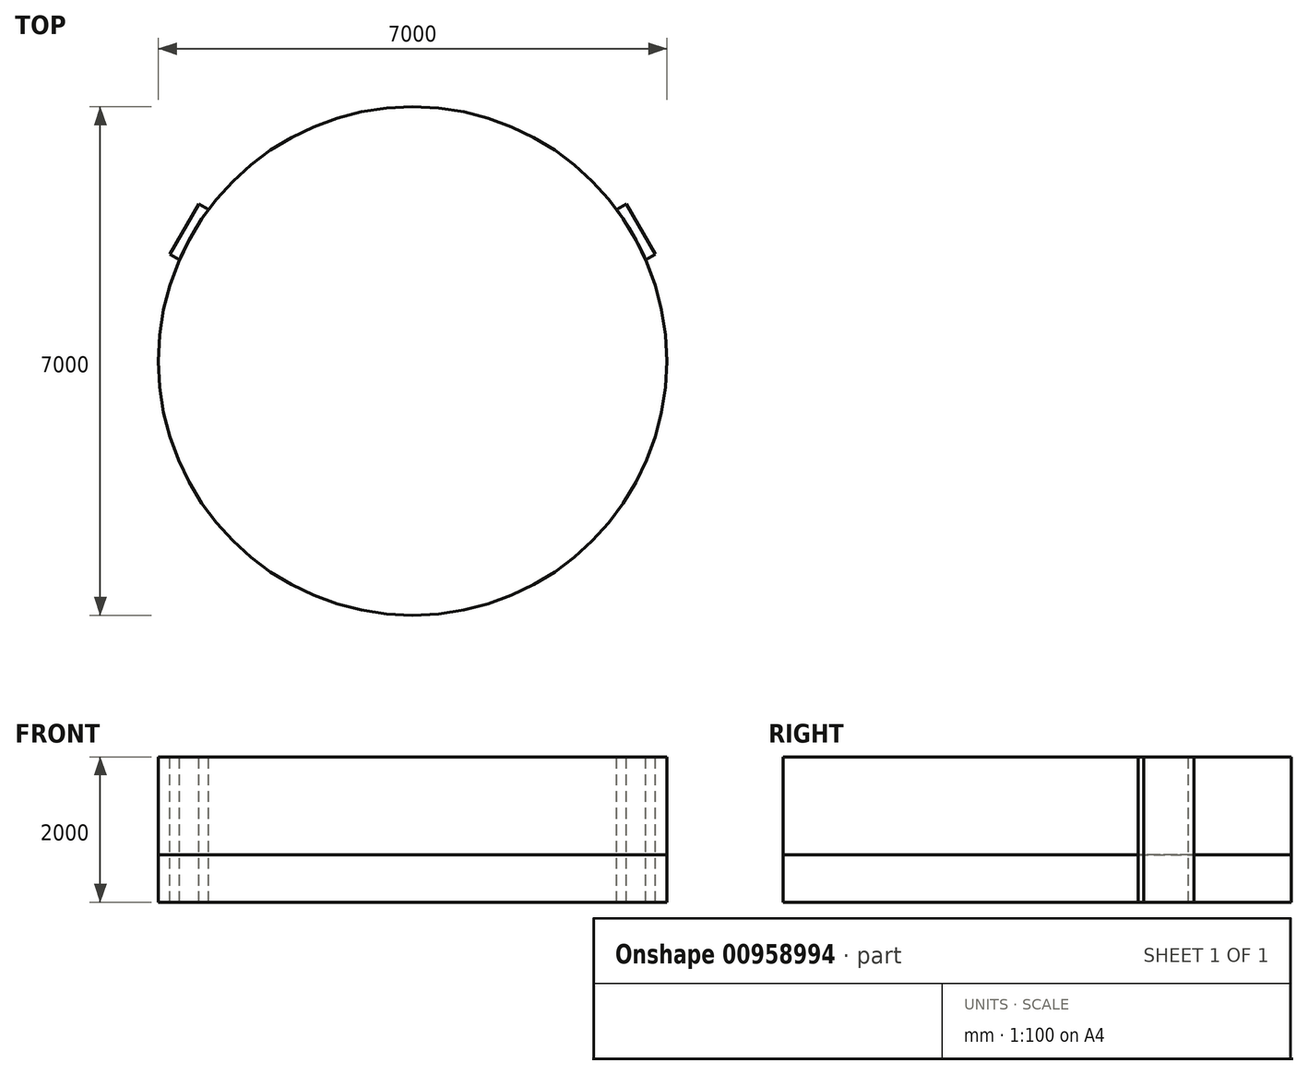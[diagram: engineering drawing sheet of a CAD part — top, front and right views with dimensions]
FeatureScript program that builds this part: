
annotation { "Feature Type Name" : "Feature", "Feature Type Description" : "" }
export const myFeature = defineFeature(function(context is Context, id is Id, definition is map)
    precondition{}
    {
        {
            var Q0;
            Q0=qCreatedBy(makeId("Top.planeOp"),FACE);
            var sketch = newSketch(context, id + "F0", { "sketchPlane" : qUnion([Q0])});
            skCircle(sketch, "E0", {"center": v(0, 0) * mm, "radius": 3500 * mm});
            skSolve(sketch);
        }
        {
            var Q0;
            Q0=makeQuery(id+"F0.imprint","IMPRINT",FACE,{"disambiguationData":[TD([[makeQuery(id+"F0.imprint","IMPRINT",EDGE,{"derivedFrom":sQuery(id+"F0.wireOp",EDGE,"E0")}),1.0]])]});
            extrude(context, id + "F1", {"entities" : qUnion([Q0]), "depth" : 1350 * mm, "offsetDistance" : 25 * mm});
        }
        {
            var Q0;
            Q0=makeQuery(id+"F1.opExtrude","CAP_FACE",FACE,{"disambiguationData":[OSD([sQuery(id+"F0.wireOp",EDGE,"E0")])],"isStart":false});
            var sketch = newSketch(context, id + "F2", { "sketchPlane" : qUnion([Q0])});
            skCircle(sketch, "E1", {"center": v(-852.5, -2750) * mm, "radius": 380 * mm});
            skLineSegment(sketch, "E2", {"start": v(-3911.37, 0) * mm, "end": v(4057.7, 0) * mm});
            skLineSegment(sketch, "E3", {"start": v(0, 3613.1) * mm, "end": v(0, -3590.58) * mm});
            skSolve(sketch);
        }
        {
            var Q0;
            Q0=sQuery(id+"F2.wireOp",EDGE,"E1");
            extrude(context, id + "F3", {"bodyType" : ToolBodyType.SURFACE, "surfaceEntities" : qUnion([Q0]), "depth" : 25 * mm, "offsetDistance" : 25 * mm});
        }
        {
            var Q0;
            Q0=makeQuery(id+"F1.opExtrude","CAP_FACE",FACE,{"disambiguationData":[OSD([sQuery(id+"F0.wireOp",EDGE,"E0")])],"isStart":false});
            var sketch = newSketch(context, id + "F4", { "sketchPlane" : qUnion([Q0])});
            skCircle(sketch, "E4", {"center": v(0, -3675.04) * mm, "radius": 110 * mm});
            skLineSegment(sketch, "E5", {"start": v(0, 3718.6) * mm, "end": v(0, -3971.3) * mm});
            skLineSegment(sketch, "E6", {"start": v(0, -3971.3) * mm, "end": v(4140.8, 0) * mm});
            skLineSegment(sketch, "E7", {"start": v(4140.8, 0) * mm, "end": v(-4000.44, 0) * mm});
            skSolve(sketch);
        }
        {
            var Q0;
            Q0=sQuery(id+"F4.wireOp",EDGE,"E4");
            extrude(context, id + "F5", {"bodyType" : ToolBodyType.SURFACE, "surfaceEntities" : qUnion([Q0]), "oppositeDirection" : true, "depth" : 2000 * mm, "offsetDistance" : 25 * mm});
        }
        {
            var Q0;
            Q0=makeQuery(id+"F1.opExtrude","CAP_FACE",FACE,{"disambiguationData":[OSD([sQuery(id+"F0.wireOp",EDGE,"E0")])],"isStart":false});
            var sketch = newSketch(context, id + "F6", { "sketchPlane" : qUnion([Q0])});
            skLineSegment(sketch, "E8", {"start": v(5183.48, 0) * mm, "end": v(-4726.63, 0) * mm});
            skLineSegment(sketch, "E9", {"start": v(0, 0) * mm, "end": v(4037.1, 2330.82) * mm});
            skLineSegment(sketch, "E10", {"start": v(0, 0) * mm, "end": v(-4709.99, 2719.31) * mm});
            skLineSegment(sketch, "E11", {"start": v(-2811.23, 2084.94) * mm, "end": v(-3211.23, 1392.12) * mm});
            skLineSegment(sketch, "E12", {"start": v(-3211.23, 1392.12) * mm, "end": v(-3341.13, 1467.12) * mm});
            skLineSegment(sketch, "E13", {"start": v(-3341.13, 1467.12) * mm, "end": v(-2941.13, 2159.94) * mm});
            skLineSegment(sketch, "E14", {"start": v(-2941.13, 2159.94) * mm, "end": v(-2811.23, 2084.94) * mm});
            skLineSegment(sketch, "E15", {"start": v(2811.23, 2084.94) * mm, "end": v(3211.23, 1392.12) * mm});
            skLineSegment(sketch, "E16", {"start": v(3211.23, 1392.12) * mm, "end": v(3341.13, 1467.12) * mm});
            skLineSegment(sketch, "E17", {"start": v(3341.13, 1467.12) * mm, "end": v(2941.13, 2159.94) * mm});
            skLineSegment(sketch, "E18", {"start": v(2941.13, 2159.94) * mm, "end": v(2811.23, 2084.94) * mm});
            skSolve(sketch);
        }
        {
            var Q0;
            {var subQ5=sQuery(id+"F6.wireOp",EDGE,"E12");Q0=makeQuery(id+"F6.imprint","IMPRINT",FACE,{"disambiguationData":[TD([[makeQuery(id+"F6.imprint","IMPRINT",EDGE,{"derivedFrom":subQ5}),-1.0]])]});}
            var Q1;
            {var subQ5=sQuery(id+"F6.wireOp",EDGE,"E14");Q1=makeQuery(id+"F6.imprint","IMPRINT",FACE,{"disambiguationData":[TD([[makeQuery(id+"F6.imprint","IMPRINT",EDGE,{"derivedFrom":subQ5}),-1.0]])]});}
            var Q2;
            {var subQ5=sQuery(id+"F6.wireOp",EDGE,"E18");Q2=makeQuery(id+"F6.imprint","IMPRINT",FACE,{"disambiguationData":[TD([[makeQuery(id+"F6.imprint","IMPRINT",EDGE,{"derivedFrom":subQ5}),1.0]])]});}
            var Q3;
            {var subQ5=sQuery(id+"F6.wireOp",EDGE,"E16");Q3=makeQuery(id+"F6.imprint","IMPRINT",FACE,{"disambiguationData":[TD([[makeQuery(id+"F6.imprint","IMPRINT",EDGE,{"derivedFrom":subQ5}),1.0]])]});}
            extrude(context, id + "F7", {"entities" : qUnion([Q0, Q1, Q2, Q3]), "oppositeDirection" : true, "depth" : 2000 * mm, "offsetDistance" : 25 * mm});
        }
        {
            var Q0;
            Q0=makeQuery(id+"F1.opExtrude","CAP_FACE",FACE,{"disambiguationData":[OSD([sQuery(id+"F0.wireOp",EDGE,"E0")])],"isStart":true});
            cPlane(context, id + "F8", {"entities" : qUnion([Q0]), "cplaneType" : CPlaneType.OFFSET, "offset" : 0 * mm, "width" : 150 * mm, "height" : 150 * mm});
        }
        {
            var Q0;
            Q0=qCreatedBy(id+"F8.planeOp",FACE);
            var sketch = newSketch(context, id + "F9", { "sketchPlane" : qUnion([Q0])});
            skCircle(sketch, "E19", {"center": v(0, 0) * mm, "radius": 3500 * mm});
            skSolve(sketch);
        }
        {
            var Q0;
            Q0 = qSketchRegion(id + "F9", true);
            extrude(context, id + "F10", {"entities" : qUnion([Q0]), "depth" : 650 * mm, "offsetDistance" : 25 * mm});
        }
    });
